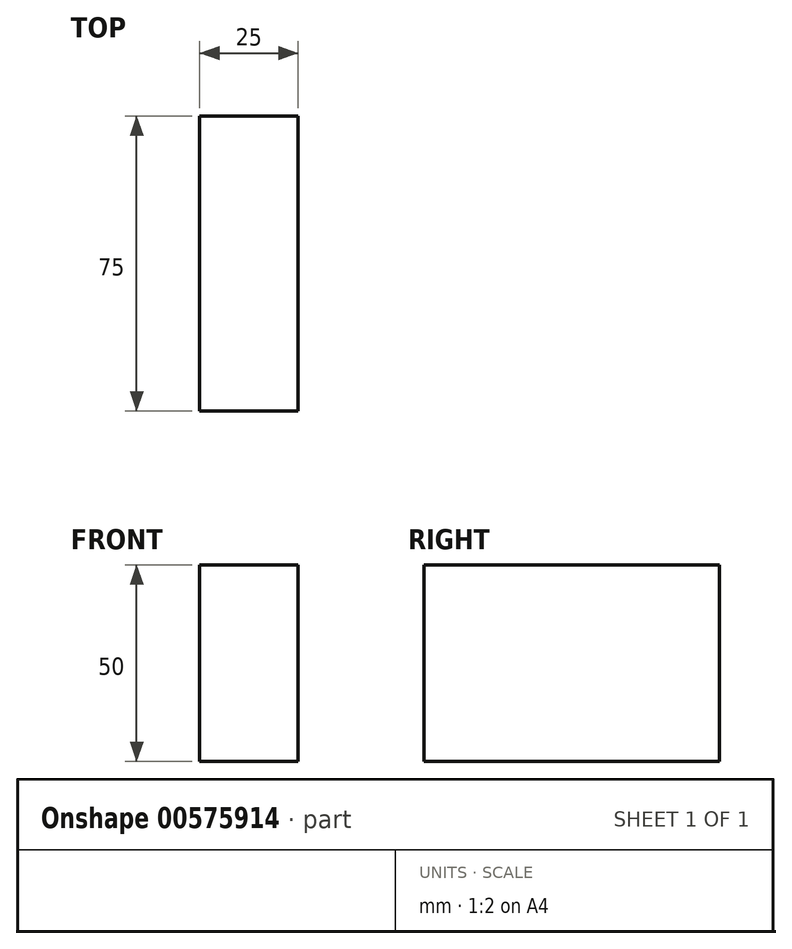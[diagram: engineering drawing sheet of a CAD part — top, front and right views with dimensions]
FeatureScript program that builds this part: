
annotation { "Feature Type Name" : "Feature", "Feature Type Description" : "" }
export const myFeature = defineFeature(function(context is Context, id is Id, definition is map)
    precondition{}
    {
        {
            var Q0;
            Q0=qCreatedBy(makeId("Front.planeOp"),FACE);
            var sketch = newSketch(context, id + "F0", { "sketchPlane" : qUnion([Q0])});
            skLineSegment(sketch, "E0.bottom", {"start": v(0, 0) * mm, "end": v(-25, 0) * mm});
            skLineSegment(sketch, "E0.top", {"start": v(0, 50) * mm, "end": v(-25, 50) * mm});
            skLineSegment(sketch, "E0.left", {"start": v(0, 0) * mm, "end": v(0, 50) * mm});
            skLineSegment(sketch, "E0.right", {"start": v(-25, 0) * mm, "end": v(-25, 50) * mm});
            skSolve(sketch);
        }
        {
            var Q0;
            Q0=makeQuery(id+"F0.imprint","IMPRINT",FACE,{"disambiguationData":[TD([[makeQuery(id+"F0.imprint","IMPRINT",EDGE,{"derivedFrom":sQuery(id+"F0.wireOp",EDGE,"E0.bottom")}),-1.0]])]});
            extrude(context, id + "F1", {"entities" : qUnion([Q0]), "depth" : 75 * mm, "offsetDistance" : 25 * mm});
        }
    });
